# Revit family: BC_RHME-(60-70)AH2_LOD400_
name_source: partatom
category: Equipement de génie climatique
revit_build: Autodesk Revit 2017 (Build: 20160225_1515(x64)
units: mm (PartAtom-declared; Revit-internal decimal feet)

## family parameters
Basée sur le plan de construction = Non
Cote de connecteur circulaire = Utiliser le diamètre
Couper avec des vides une fois chargée = Non
Numéro OmniClass = 23.75.10.24
Partagée = Non
Point de calcul de pièce = Non
Titre OmniClass = Cooling and Freeze Plant
Toujours verticalement = Oui
Type d'élément = Normal

## types (2) — shared parameters
Coefficient Of Performance (COP) = 2.82
Color = Natural Grey
Commentaires du type = Samurai - Air Cooled Heat Pump - RHME 70AH2
Description = Samurai - Air Cooled Heat Pump
Energy Efficiency Ratio (EER) = 2.93
Fabricant = HITACHI
Heating Capacity = 145 kW
Heating Nominal Current = 89 A
Heating Nominal Flow = 24.9 m³/h
Heating Nominal Input Power = 51 kW
Heating Power = 52 kW
Inlet Water Diameter = 368 mm
Maximum AC Voltage = 440 V
Maximum Air Flow = 50.4 m³/h
Maximum Starting Current for cable sizing = 240 A
Minimum AC Voltage = 360 V
Modèle = Samurai - Air Cooled Heat Pump
Nominal Voltage = 400 V
Operating Mode Heat Pump = Heat Pump (5)
Overall Height = 2450 mm
Overall Length = 2290 mm
Overall Width = 1955 mm
Rated Frequency = 50 Hz
Refrigerant Type = R134a
Season Coefficient Of Performance (SCOP) = 3.22
Seasonal Energy Efficiency Ratio (SEER) = 3.88
Starting Current = 240 A
Static Pressure = 0.0 kPa
Water Outlet Diameter = 368 mm

## per-type parameters (varying)
- Samurai - Air Cooled Heat Pump - RHME 60AH2: AXI_PDS_FCT=1400.00 kg; Cooling Airflow High=36.9 m³/h; Cooling Capacity=150 kW; Cooling Capacity Min=16 kW; Cooling Nominal Current=88 A; Cooling Nominal Flow=25.8 m³/h; Cooling Nominal Input Power=51 kW; Cooling Power=51 kW; Cooling Pressure Drop at nominal flow=11.4 kPa; Extra Super Low Noise Model (dB(A))=88; Extra Super Low Noise Model at 10m (dB(A))=60; Heating Airflow High=36.9 m³/h; Heating Capacity Min=16 kW; Heating Pressure Drop at nominal flow=10.7 kPa; Heating Sound Level Low (dB)=93; Heating Sound Level Silent (dB)=96; Low Noise Model at 10m (dB(A))=65; Maximum Current for cable sizing=119 A; Maximum Input Power for cable sizing=69 kW; Nominal Current=88 A; Product Code=9E061342; Refrigerant Quantity=37.00 kg; Standard Noise Level Model at 10m (dB(A))=68; Super Low Noise Model (dB(A))=91; Super Low Noise Model at 10m (dB(A))=63; Weight Packing=1380.00 kg
- Samurai - Air Cooled Heat Pump - RHME 70AH2: AXI_PDS_FCT=1420.00 kg; Cooling Airflow High=41.8 m³/h; Cooling Capacity=170 kW; Cooling Capacity Min=18 kW; Cooling Nominal Current=99 A; Cooling Nominal Flow=29.2 m³/h; Cooling Nominal Input Power=58 kW; Cooling Power=58 kW; Cooling Pressure Drop at nominal flow=14.3 kPa; Extra Super Low Noise Model (dB(A))=89; Extra Super Low Noise Model at 10m (dB(A))=61; Heating Airflow High=41.8 m³/h; Heating Capacity Min=18 kW; Heating Pressure Drop at nominal flow=0.0 kPa; Heating Sound Level Low (dB)=94; Heating Sound Level Silent (dB)=97; Low Noise Model at 10m (dB(A))=66; Maximum Current for cable sizing=133 A; Maximum Input Power for cable sizing=78 kW; Nominal Current=99 A; Product Code=9E071342; Refrigerant Quantity=39.00 kg; Standard Noise Level Model at 10m (dB(A))=69; Super Low Noise Model (dB(A))=92; Super Low Noise Model at 10m (dB(A))=64; Weight Packing=1400.00 kg
